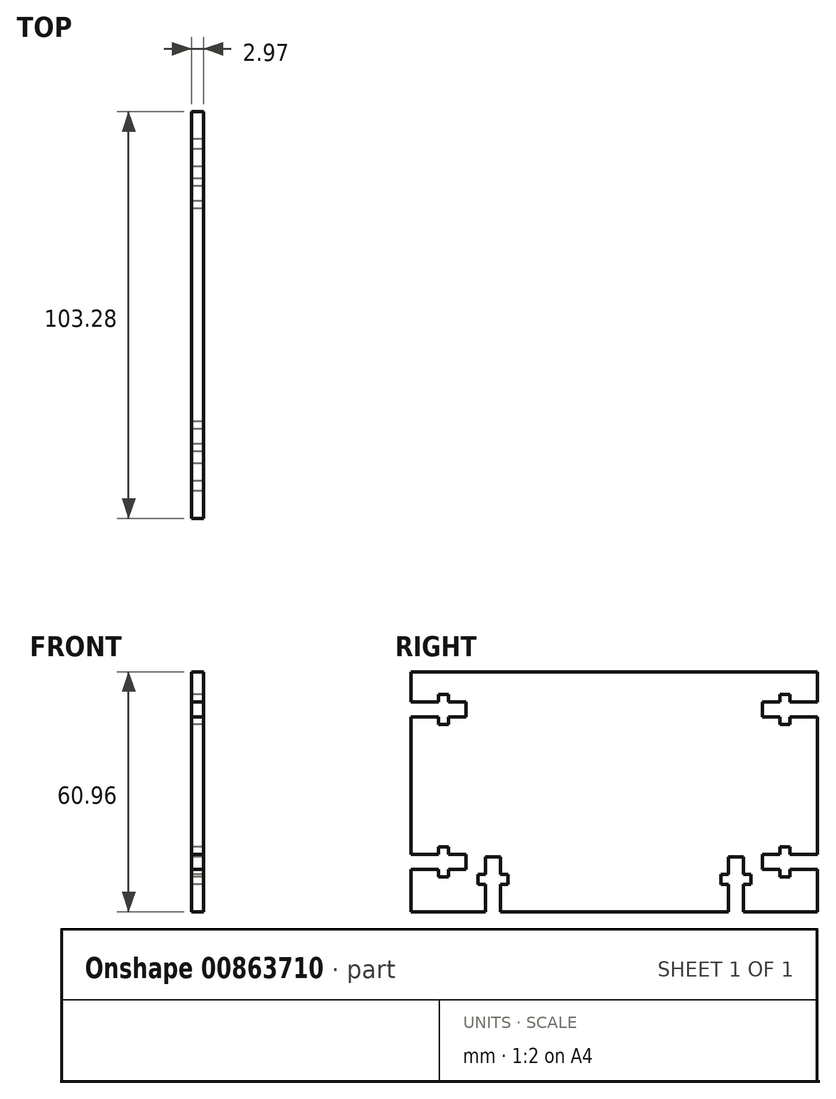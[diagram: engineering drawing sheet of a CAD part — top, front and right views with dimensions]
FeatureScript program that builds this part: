
annotation { "Feature Type Name" : "Feature", "Feature Type Description" : "" }
export const myFeature = defineFeature(function(context is Context, id is Id, definition is map)
    precondition{}
    {
        {
            var Q0;
            Q0=qCreatedBy(makeId("Right.planeOp"),FACE);
            var sketch = newSketch(context, id + "F0", { "sketchPlane" : qUnion([Q0])});
            skLineSegment(sketch, "E0.bottom", {"start": v(0, 0) * mm, "end": v(18.85, 0) * mm});
            skLineSegment(sketch, "E0.left", {"start": v(0, 0) * mm, "end": v(0, 10.8) * mm});
            skLineSegment(sketch, "E0.right", {"start": v(103.28, 0) * mm, "end": v(103.28, 10.8) * mm});
            skLineSegment(sketch, "E1", {"start": v(0, 60.96) * mm, "end": v(103.28, 60.96) * mm});
            skLineSegment(sketch, "E2", {"start": v(103.28, 60.96) * mm, "end": v(103.28, 60.96) * mm});
            skLineSegment(sketch, "E3", {"start": v(0, 53.34) * mm, "end": v(6.99, 53.34) * mm});
            skLineSegment(sketch, "E4", {"start": v(6.99, 53.34) * mm, "end": v(6.99, 55.24) * mm});
            skLineSegment(sketch, "E5", {"start": v(6.99, 55.24) * mm, "end": v(9.53, 55.24) * mm});
            skLineSegment(sketch, "E6", {"start": v(9.53, 55.24) * mm, "end": v(9.53, 53.34) * mm});
            skLineSegment(sketch, "E7", {"start": v(9.53, 53.34) * mm, "end": v(13.97, 53.34) * mm});
            skLineSegment(sketch, "E8", {"start": v(13.97, 53.34) * mm, "end": v(13.97, 49.53) * mm});
            skLineSegment(sketch, "E9", {"start": v(13.97, 49.53) * mm, "end": v(9.53, 49.53) * mm});
            skLineSegment(sketch, "E10", {"start": v(9.53, 49.53) * mm, "end": v(9.53, 47.62) * mm});
            skLineSegment(sketch, "E11", {"start": v(9.53, 47.62) * mm, "end": v(6.99, 47.62) * mm});
            skLineSegment(sketch, "E12", {"start": v(6.99, 47.62) * mm, "end": v(6.99, 49.53) * mm});
            skLineSegment(sketch, "E13", {"start": v(6.99, 49.53) * mm, "end": v(0, 49.53) * mm});
            skLineSegment(sketch, "E14.trimOffspring", {"start": v(0, 53.34) * mm, "end": v(0, 60.96) * mm});
            skLineSegment(sketch, "E15", {"start": v(0, 14.6) * mm, "end": v(6.98, 14.6) * mm});
            skLineSegment(sketch, "E16", {"start": v(6.98, 14.6) * mm, "end": v(6.98, 16.5) * mm});
            skLineSegment(sketch, "E17", {"start": v(6.98, 16.5) * mm, "end": v(9.53, 16.5) * mm});
            skLineSegment(sketch, "E18", {"start": v(9.53, 16.5) * mm, "end": v(9.53, 14.6) * mm});
            skLineSegment(sketch, "E19", {"start": v(9.53, 14.6) * mm, "end": v(13.97, 14.6) * mm});
            skLineSegment(sketch, "E20", {"start": v(13.97, 14.6) * mm, "end": v(13.97, 10.8) * mm});
            skLineSegment(sketch, "E21", {"start": v(13.97, 10.8) * mm, "end": v(9.53, 10.8) * mm});
            skLineSegment(sketch, "E22", {"start": v(9.53, 10.8) * mm, "end": v(9.53, 8.89) * mm});
            skLineSegment(sketch, "E23", {"start": v(9.53, 8.89) * mm, "end": v(6.98, 8.89) * mm});
            skLineSegment(sketch, "E24", {"start": v(6.98, 8.89) * mm, "end": v(6.98, 10.8) * mm});
            skLineSegment(sketch, "E25", {"start": v(6.98, 10.8) * mm, "end": v(0, 10.8) * mm});
            skLineSegment(sketch, "E26.trimOffspring", {"start": v(0, 14.6) * mm, "end": v(0, 49.53) * mm});
            skLineSegment(sketch, "E27", {"start": v(51.64, 0) * mm, "end": v(51.64, 60.96) * mm, "construction": true});
            skLineSegment(sketch, "E28.MirrorCS", {"start": v(103.28, 53.34) * mm, "end": v(96.3, 53.34) * mm});
            skLineSegment(sketch, "E29.MirrorCS", {"start": v(96.3, 53.34) * mm, "end": v(96.3, 55.25) * mm});
            skLineSegment(sketch, "E30.MirrorCS", {"start": v(96.3, 55.24) * mm, "end": v(93.75, 55.24) * mm});
            skLineSegment(sketch, "E31.MirrorCS", {"start": v(93.75, 55.25) * mm, "end": v(93.75, 53.34) * mm});
            skLineSegment(sketch, "E32.MirrorCS", {"start": v(93.75, 53.34) * mm, "end": v(89.3, 53.34) * mm});
            skLineSegment(sketch, "E33.MirrorCS", {"start": v(89.3, 53.34) * mm, "end": v(89.3, 49.53) * mm});
            skLineSegment(sketch, "E34.MirrorCS", {"start": v(89.3, 49.53) * mm, "end": v(93.75, 49.53) * mm});
            skLineSegment(sketch, "E35.MirrorCS", {"start": v(93.75, 49.53) * mm, "end": v(93.75, 47.63) * mm});
            skLineSegment(sketch, "E36.MirrorCS", {"start": v(93.75, 47.63) * mm, "end": v(96.3, 47.63) * mm});
            skLineSegment(sketch, "E37.MirrorCS", {"start": v(96.3, 47.63) * mm, "end": v(96.3, 49.53) * mm});
            skLineSegment(sketch, "E38.MirrorCS", {"start": v(96.3, 49.53) * mm, "end": v(103.28, 49.53) * mm});
            skLineSegment(sketch, "E39.MirrorCS", {"start": v(103.28, 14.6) * mm, "end": v(96.3, 14.6) * mm});
            skLineSegment(sketch, "E40.MirrorCS", {"start": v(96.3, 14.6) * mm, "end": v(96.3, 16.5) * mm});
            skLineSegment(sketch, "E41.MirrorCS", {"start": v(96.3, 16.5) * mm, "end": v(93.75, 16.5) * mm});
            skLineSegment(sketch, "E42.MirrorCS", {"start": v(93.75, 16.5) * mm, "end": v(93.75, 14.6) * mm});
            skLineSegment(sketch, "E43.MirrorCS", {"start": v(93.75, 14.6) * mm, "end": v(89.3, 14.6) * mm});
            skLineSegment(sketch, "E44.MirrorCS", {"start": v(89.3, 14.6) * mm, "end": v(89.3, 10.8) * mm});
            skLineSegment(sketch, "E45.MirrorCS", {"start": v(89.3, 10.8) * mm, "end": v(93.75, 10.8) * mm});
            skLineSegment(sketch, "E46.MirrorCS", {"start": v(93.75, 10.8) * mm, "end": v(93.75, 8.89) * mm});
            skLineSegment(sketch, "E47.MirrorCS", {"start": v(93.75, 8.89) * mm, "end": v(96.3, 8.89) * mm});
            skLineSegment(sketch, "E48.MirrorCS", {"start": v(96.3, 8.89) * mm, "end": v(96.3, 10.8) * mm});
            skLineSegment(sketch, "E49.MirrorCS", {"start": v(96.3, 10.8) * mm, "end": v(103.28, 10.8) * mm});
            skLineSegment(sketch, "E50.trimOffspring", {"start": v(103.28, 53.34) * mm, "end": v(103.28, 60.96) * mm});
            skLineSegment(sketch, "E51.trimOffspring", {"start": v(103.28, 14.6) * mm, "end": v(103.28, 49.53) * mm});
            skLineSegment(sketch, "E52", {"start": v(18.85, 0) * mm, "end": v(18.85, 6.98) * mm});
            skLineSegment(sketch, "E53", {"start": v(18.85, 6.98) * mm, "end": v(16.94, 6.98) * mm});
            skLineSegment(sketch, "E54", {"start": v(16.94, 6.98) * mm, "end": v(16.94, 9.52) * mm});
            skLineSegment(sketch, "E55", {"start": v(16.94, 9.52) * mm, "end": v(18.85, 9.52) * mm});
            skLineSegment(sketch, "E56", {"start": v(18.85, 9.52) * mm, "end": v(18.85, 13.97) * mm});
            skLineSegment(sketch, "E57", {"start": v(18.85, 13.97) * mm, "end": v(22.66, 13.97) * mm});
            skLineSegment(sketch, "E58", {"start": v(22.66, 13.97) * mm, "end": v(22.66, 9.52) * mm});
            skLineSegment(sketch, "E59", {"start": v(22.66, 9.52) * mm, "end": v(24.56, 9.52) * mm});
            skLineSegment(sketch, "E60", {"start": v(24.56, 9.52) * mm, "end": v(24.56, 6.98) * mm});
            skLineSegment(sketch, "E61", {"start": v(24.56, 6.98) * mm, "end": v(22.66, 6.98) * mm});
            skLineSegment(sketch, "E62", {"start": v(22.66, 6.98) * mm, "end": v(22.66, 0) * mm});
            skLineSegment(sketch, "E63.trimOffspring", {"start": v(22.66, 0) * mm, "end": v(80.62, 0) * mm});
            skLineSegment(sketch, "E64.MirrorCS", {"start": v(84.43, 0) * mm, "end": v(84.43, 6.98) * mm});
            skLineSegment(sketch, "E65.MirrorCS", {"start": v(84.43, 6.98) * mm, "end": v(86.33, 6.98) * mm});
            skLineSegment(sketch, "E66.MirrorCS", {"start": v(86.33, 6.98) * mm, "end": v(86.33, 9.52) * mm});
            skLineSegment(sketch, "E67.MirrorCS", {"start": v(86.33, 9.52) * mm, "end": v(84.43, 9.52) * mm});
            skLineSegment(sketch, "E68.MirrorCS", {"start": v(84.43, 9.52) * mm, "end": v(84.43, 13.97) * mm});
            skLineSegment(sketch, "E69.MirrorCS", {"start": v(84.43, 13.97) * mm, "end": v(80.62, 13.97) * mm});
            skLineSegment(sketch, "E70.MirrorCS", {"start": v(80.62, 13.97) * mm, "end": v(80.62, 9.52) * mm});
            skLineSegment(sketch, "E71.MirrorCS", {"start": v(80.62, 9.52) * mm, "end": v(78.71, 9.52) * mm});
            skLineSegment(sketch, "E72.MirrorCS", {"start": v(78.71, 9.52) * mm, "end": v(78.71, 6.98) * mm});
            skLineSegment(sketch, "E73.MirrorCS", {"start": v(78.71, 6.98) * mm, "end": v(80.62, 6.98) * mm});
            skLineSegment(sketch, "E74.MirrorCS", {"start": v(80.62, 6.98) * mm, "end": v(80.62, 0) * mm});
            skLineSegment(sketch, "E75.trimOffspring", {"start": v(84.43, 0) * mm, "end": v(103.28, 0) * mm});
            skSolve(sketch);
        }
        {
            var Q0;
            Q0 = qSketchRegion(id + "F0", true);
            extrude(context, id + "F1", {"entities" : qUnion([Q0]), "depth" : 2.97 * mm, "offsetDistance" : 25.4 * mm});
        }
    });
